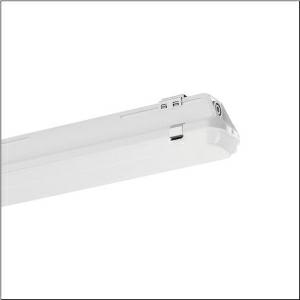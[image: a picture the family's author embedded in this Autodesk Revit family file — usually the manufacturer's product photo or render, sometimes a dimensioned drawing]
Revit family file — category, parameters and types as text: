
# Revit family: monsun_r__21_51fb107p420b_fb8a
name_source: partatom
category: Lighting Fixtures
units: mm (PartAtom-declared; Revit-internal decimal feet)

## family parameters
Cut with Voids When Loaded = No
Host = Face
Light Source = No
Part Type = Normal
Room Calculation Point = No
Round Connector Dimension = Use Diameter
Shared = No

## types (1)
- Monsun® 21 (1 x LED, 2580 lm, 17.5 W, 4000K)
    Apparent Load = 18 VA
    CIE Flux Codes = 47 77 93 94 100
    Color Rendering = 80
    Color Temperature = 4000K
    Default Elevation = 1800 mm
    Description = Monsun® 21, damp-proof luminaire, chain hanger, primary optical cover: enclosure, of PMMA, light emission: direct distribution, primary light characteristic: symmetric, installation type: suspended mounting, surface-mounted, horizontal mounting, vertical mounting, LED, rated luminous flux: 2.580lm, luminous efficacy: 147lm/W, light colour: 840, colour temperature: 4000K, control gear: ECG, with terminal, 3-pole, max. 2.5mm², mains connection: 220..240V, AC, 50/60Hz, rated input power: 18W, housing, of glass-fibre reinforced polyester, uncoated, bright grey, length: 1.590mm, width: 90mm, height: 88mm, clip for enclosure, of stainless steel (V2A), ceiling mounting element, of stainless steel (V2A), chain hanger, of stainless steel (V2A), protection rating (complete): IP66, insulation class (complete): insulation class I (protective earthing), certification: CE, ENEC, VDE, UKCA, protection symbol: D, impact resistance: IK04, permissible operating ambient temperature: -25..+35°C, standard: EN 50419, EN 60598-2-1, corresponds to IFS (International Featured Standards) requirements for safety and quality in the food industry, for indoor or canopied outdoor use, no direct snow, no direct sun, no direct rain, packaging unit: 1 piece
    Height = 89 mm
    Lamp = 1 x LED
    Lamp Light Flux = 2580 lm
    Lamp Power = 17.5 W
    Lamp count = 1
    Length = 1590 mm
    Luminous efficacy = 147 lm/W
    Manufacturer = Siteco
    ModVariant = No
    Model = 51FB107P420B
    Mounting Place = Ceiling
    Mounting Type = Pendant
    Number of Poles = 1
    OnlyDefault = Yes
    Power Factor = 1
    Product Name = Monsun® 21
    Product group = damp-proof luminaire | ceiling pendant
    ProductGroupID = 908
    Protection Class = Protection class I
    Protection Degree = IP 66
    RLX_Detail_Level = 1
    RlxData = <blob elided: 88013 chars, md5=7a71d16e>
    Socket = socket
    Standby Power = 0 W
    System Light Flux = 2580 lm
    System Power = 18 W
    Type Comments = Product without accessories
    Type Image = l_1006717.jpg
    URL = http://relux.com
    VarID = ---
    Voltage = 0 V
    Weight = 0.00 kg
    Width = 90 mm

## geometry (parser evidence)
native form markers: Blend x4, Sweep x13
no freeform markers — native parametric forms only
